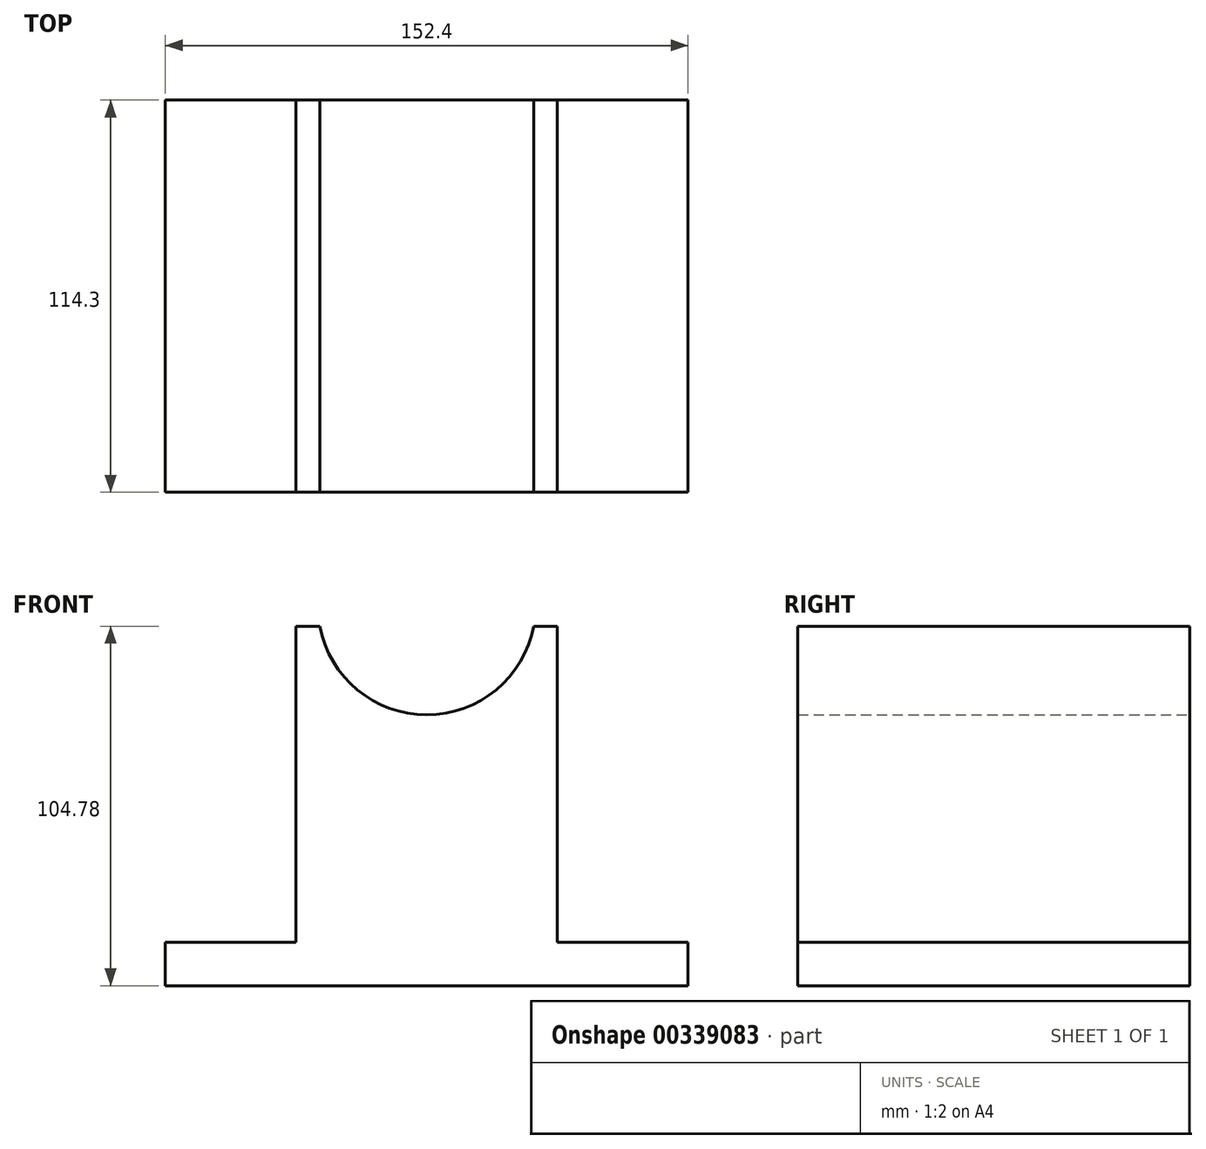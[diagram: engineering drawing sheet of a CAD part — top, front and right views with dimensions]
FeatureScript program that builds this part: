
annotation { "Feature Type Name" : "Feature", "Feature Type Description" : "" }
export const myFeature = defineFeature(function(context is Context, id is Id, definition is map)
    precondition{}
    {
        {
            var Q0;
            Q0=qCreatedBy(makeId("Front.planeOp"),FACE);
            var sketch = newSketch(context, id + "F0", { "sketchPlane" : qUnion([Q0])});
            skLineSegment(sketch, "E0", {"start": v(-77.75, -65.48) * mm, "end": v(74.65, -65.48) * mm});
            skLineSegment(sketch, "E1", {"start": v(74.65, -65.48) * mm, "end": v(74.65, -52.78) * mm});
            skLineSegment(sketch, "E2", {"start": v(74.65, -52.78) * mm, "end": v(36.55, -52.78) * mm});
            skLineSegment(sketch, "E3", {"start": v(36.55, -52.78) * mm, "end": v(36.55, 39.3) * mm});
            skLineSegment(sketch, "E4", {"start": v(36.55, 39.3) * mm, "end": v(29.64, 39.3) * mm});
            skLineSegment(sketch, "E5", {"start": v(-77.75, -65.48) * mm, "end": v(-77.75, -52.78) * mm});
            skLineSegment(sketch, "E6", {"start": v(-77.75, -52.78) * mm, "end": v(-39.65, -52.78) * mm});
            skLineSegment(sketch, "E7", {"start": v(-39.65, -52.78) * mm, "end": v(-39.65, 39.3) * mm});
            skLineSegment(sketch, "E8", {"start": v(-39.65, 39.3) * mm, "end": v(-32.75, 39.3) * mm});
            skArc(sketch, "E9", {"start": v(-32.75, 39.3) * mm, "mid": v(-1.55, 13.44) * mm, "end": v(29.64, 39.3) * mm});
            skSolve(sketch);
        }
        {
            var Q0;
            Q0=makeQuery(id+"F0.imprint","IMPRINT",FACE,{"disambiguationData":[TD([[makeQuery(id+"F0.imprint","IMPRINT",EDGE,{"derivedFrom":sQuery(id+"F0.wireOp",EDGE,"E0")}),1.0]])]});
            extrude(context, id + "F1", {"entities" : qUnion([Q0]), "depth" : 114.3 * mm, "symmetric" : true});
        }
    });
